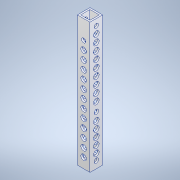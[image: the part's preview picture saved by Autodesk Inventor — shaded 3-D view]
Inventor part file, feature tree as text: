
AUTODESK INVENTOR PART (.ipt)
format: ipt  version: 2020.3 (Build 243373000, 373)  size: 271,872 bytes
history: native  units: mm
features: sketch x8, hole x7, other x1, extrude x1
ambient origin geometry x8: Origin, YZ Plane, XZ Plane, XY Plane, X Axis, Y Axis, Z Axis, Center Point
bodies: Body1 (feature_tree)
feature tree (17):
  other  "ソリッド1"
  extrude  "押し出し1"  Depth=9.0mm
  hole  "穴1"  [1 undecoded]
  hole  "穴4"  [1 undecoded]
  hole  "穴5"  [1 undecoded]
  hole  "穴6"  [1 undecoded]
  hole  "穴7"  [1 undecoded]
  hole  "穴8"  [1 undecoded]
  hole  "穴9"  [1 undecoded]
  sketch  "スケッチ1"
  sketch  "スケッチ2"
  sketch  "スケッチ5"
  sketch  "スケッチ6"
  sketch  "スケッチ7"
  sketch  "スケッチ8"
  sketch  "スケッチ9"
  sketch  "スケッチ10"
note: 7 required parameter values undecoded (feature->parameter linkage not recoverable at this tier; creation-order binding heuristic only, values carry confidence <= 0.55)
